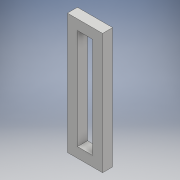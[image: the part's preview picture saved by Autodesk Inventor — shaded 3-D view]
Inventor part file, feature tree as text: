
AUTODESK INVENTOR PART (.ipt)
format: ipt  version: 2017 (Build 210142000, 142)  size: 97,280 bytes
history: native  units: mm
features: extrude x1, sketch x1
ambient origin geometry x8: Origin, YZ Plane, XZ Plane, XY Plane, X Axis, Y Axis, Z Axis, Center Point
bodies: Solid1 (feature_tree)
feature tree (2):
  extrude  "Extrusion1"  Depth=20.0mm
  sketch  "Sketch1"  dims[d0=3.0mm d1=20.0mm d2=2.0mm d3=2.0mm d4=0.0mm]
